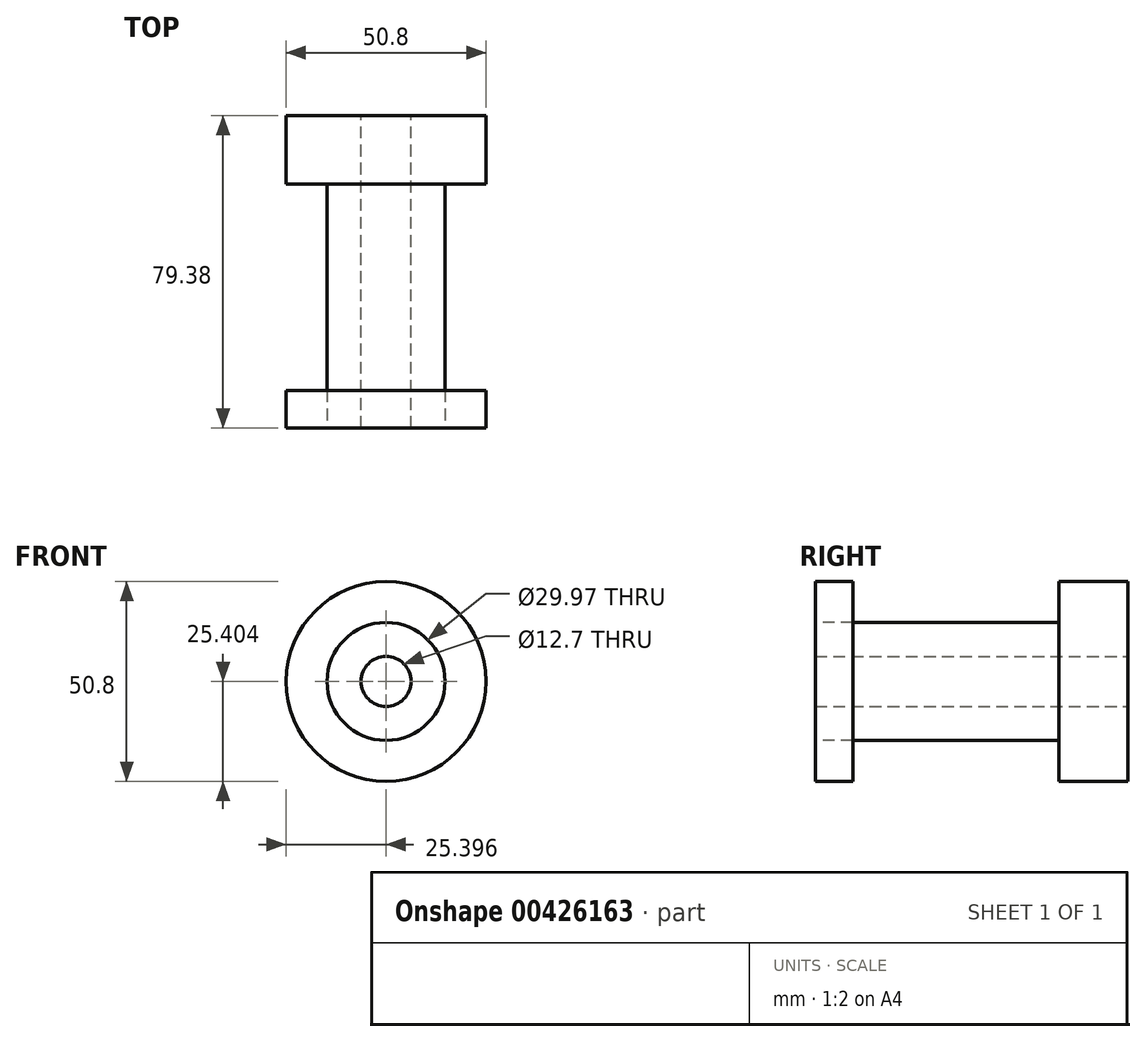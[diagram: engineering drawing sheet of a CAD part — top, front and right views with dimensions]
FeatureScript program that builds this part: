
annotation { "Feature Type Name" : "Feature", "Feature Type Description" : "" }
export const myFeature = defineFeature(function(context is Context, id is Id, definition is map)
    precondition{}
    {
        {
            var Q0;
            Q0=qCreatedBy(makeId("Front.planeOp"),FACE);
            var sketch = newSketch(context, id + "F0", { "sketchPlane" : qUnion([Q0])});
            skCircle(sketch, "E0", {"center": v(-25.05, 20.2) * mm, "radius": 25.4 * mm});
            skSolve(sketch);
        }
        {
            var Q0;
            Q0=makeQuery(id+"F0.imprint","IMPRINT",FACE,{"disambiguationData":[TD([[makeQuery(id+"F0.imprint","IMPRINT",EDGE,{"derivedFrom":sQuery(id+"F0.wireOp",EDGE,"E0")}),1.0]])]});
            extrude(context, id + "F1", {"entities" : qUnion([Q0]), "depth" : 17.46 * mm});
        }
        {
            var Q0;
            Q0=makeQuery(id+"F1.opExtrude","CAP_FACE",FACE,{"disambiguationData":[OSD([sQuery(id+"F0.wireOp",EDGE,"E0")])],"isStart":false});
            var sketch = newSketch(context, id + "F2", { "sketchPlane" : qUnion([Q0])});
            skCircle(sketch, "E1", {"center": v(-25.05, 20.2) * mm, "radius": 14.99 * mm});
            skSolve(sketch);
        }
        {
            var Q0;
            Q0=makeQuery(id+"F2.imprint","IMPRINT",FACE,{"disambiguationData":[TD([[makeQuery(id+"F2.imprint","IMPRINT",EDGE,{"derivedFrom":sQuery(id+"F2.wireOp",EDGE,"E1")}),1.0]])]});
            extrude(context, id + "F3", {"entities" : qUnion([Q0]), "operationType" : NewBodyOperationType.ADD, "depth" : 61.9 * mm});
        }
        {
            var Q0;
            Q0=makeQuery(id+"F3.opExtrude","CAP_FACE",FACE,{"disambiguationData":[OSD([sQuery(id+"F2.wireOp",EDGE,"E1")])],"isStart":false});
            var sketch = newSketch(context, id + "F4", { "sketchPlane" : qUnion([Q0])});
            skCircle(sketch, "E2", {"center": v(-25.05, 20.2) * mm, "radius": 25.4 * mm});
            skSolve(sketch);
        }
        {
            var Q0;
            Q0=makeQuery(id+"F4.imprint","IMPRINT",FACE,{"disambiguationData":[TD([[makeQuery(id+"F4.imprint","IMPRINT",EDGE,{"derivedFrom":sQuery(id+"F4.wireOp",EDGE,"E2")}),1.0]])]});
            extrude(context, id + "F5", {"entities" : qUnion([Q0]), "oppositeDirection" : true, "depth" : 9.52 * mm});
        }
        {
            var Q0;
            Q0=makeQuery(id+"F1.opExtrude","CAP_FACE",FACE,{"disambiguationData":[OSD([sQuery(id+"F0.wireOp",EDGE,"E0")])],"isStart":true});
            var sketch = newSketch(context, id + "F6", { "sketchPlane" : qUnion([Q0])});
            skCircle(sketch, "E3", {"center": v(25.05, 20.2) * mm, "radius": 6.35 * mm});
            skSolve(sketch);
        }
        {
            var Q0;
            Q0=makeQuery(id+"F6.imprint","IMPRINT",FACE,{"disambiguationData":[TD([[makeQuery(id+"F6.imprint","IMPRINT",EDGE,{"derivedFrom":sQuery(id+"F6.wireOp",EDGE,"E3")}),1.0]])]});
            extrude(context, id + "F7", {"entities" : qUnion([Q0]), "operationType" : NewBodyOperationType.REMOVE, "endBound" : BoundingType.THROUGH_ALL, "oppositeDirection" : true, "depth" : 25.4 * mm});
        }
    });
